# Revit family: Toilet-Waterworks-Alden
name_source: partatom
category: Plumbing Fixtures
revit_build: Autodesk Revit MEP 2014 (Build: 20140709_2115(x64)
units: mm (PartAtom-declared; Revit-internal decimal feet)

## types (24) — shared parameters
ADA Compliant = Yes
Assembly Code = D2010110
CW Connection = Yes
Certification IAPMO = Yes
Certification Watersense = Yes
Certification cUPC = Yes
Code Compliance = Complies with ASME 112.19.2-2008/CSA B45.1-08, WaterSense. Certified with IAPMO & cUPC
Cold Water Connector = Cold Water - Male Threading
Cold Water Diameter = 0' - 0 1/2"
Default Elevation = 0' - 0"
Depth = 2' - 5 1/4"
Flush Rate = 1.28 gpf
HW Connection = No
Height = 2' - 3 5/8"
Keynote = 22 40 00.E3
Length = 1' - 4 1/4"
Manufacturer = Waterworks
Model = ALWC01
Pressure = 45.00 psi
Product Documentation Link = http://assets.waterworks.com
Product Name = Alden One Piece High Efficiency Elongated Watercloset with Molded Wood Seat
Product Page URL = http://www.waterworks.com
Sanitary Connector = Waste Drain
Trapway Diameter = 0' - 2 1/8"
URL = http://www.waterworks.com
Vent Connection = Yes
Version = 2014 - v1.0a
Warranty = http://www.waterworks.com
Waste Connection = Yes
Waste Connection Diameter = 0' - 2 1/8"
Water Pressure = Max: 85psi / Min: 20psi / Recommended: 45psi
‌Installation Requirements or Notes = Waste Rough-In Depth: 1-2in from finished wall.  See Installation Guidelines

## per-type parameters (varying)
| type | Constraint | Description | Finish | Metal Finish | Model SKU |
| Bright White - Antique Brass  Lever | 1 | One Piece Elongated Watercloset in Bright White with Antique Brass Lever | Vitreous China - Waterworks - Bright White | Metal - Waterworks - Antique Brass | 14-08039-64466 |
| Bright White - Antique Copper  Lever | 2 | One Piece Elongated Watercloset in Bright White with Antique Copper Lever | Vitreous China - Waterworks - Bright White | Metal - Waterworks - Antique Copper | 14-01136-13871 |
| Bright White - Architectural Bronze  Lever | 3 | One Piece Elongated Watercloset in Bright White with Architectural Bronze Lever | Vitreous China - Waterworks - Bright White | Metal - Waterworks - Architectural Bronze | 14-38638-51317 |
| Bright White - Burnished Brass  Lever | 4 | One Piece Elongated Watercloset in Bright White with Burnished Brass Lever | Vitreous China - Waterworks - Bright White | Metal - Waterworks - Burnished Brass | 14-32651-23069 |
| Bright White - Burnished Nickel  Lever | 5 | One Piece Elongated Watercloset in Bright White with Burnished Nickel Lever | Vitreous China - Waterworks - Bright White | Metal - Waterworks - Burnished Nickel | 14-56783-33394 |
| Bright White - Carbon  Lever | 6 | One Piece Elongated Watercloset in Bright White with Carbon Lever | Vitreous China - Waterworks - Bright White | Metal - Waterworks - Carbon | 14-89032-34872 |
| Bright White - Chrome  Lever | 7 | One Piece Elongated Watercloset in Bright White with Chrome Lever | Vitreous China - Waterworks - Bright White | Metal - Waterworks - Chrome | 14-48096-60456 |
| Bright White - Gold  Lever | 8 | One Piece Elongated Watercloset in Bright White with Gold Lever | Vitreous China - Waterworks - Bright White | Metal - Waterworks - Gold | 14-45384-68425 |
| Bright White - Matte Gold  Lever | 9 | One Piece Elongated Watercloset in Bright White with Matte Gold Lever | Vitreous China - Waterworks - Bright White | Metal - Waterworks - Matte Gold | 14-83029-59346 |
| Bright White - Matte Nickel  Lever | 10 | One Piece Elongated Watercloset in Bright White with Matte Nickel Lever | Vitreous China - Waterworks - Bright White | Metal - Waterworks - Matte Nickel | 14-23729-66657 |
| Bright White - Nickel  Lever | 11 | One Piece Elongated Watercloset in Bright White with Nickel Lever | Vitreous China - Waterworks - Bright White | Metal - Waterworks - Nickel | 14-67965-18117 |
| Bright White - Pewter  Lever | 12 | One Piece Elongated Watercloset in Bright White with Pewter Lever | Vitreous China - Waterworks - Bright White | Metal - Waterworks - Pewter | 14-19227-72516 |
| Bright White - Shiny Copper  Lever | 13 | One Piece Elongated Watercloset in Bright White with Shiny Copper Lever | Vitreous China - Waterworks - Bright White | Metal - Waterworks - Shiny Copper | 14-49333-08937 |
| Bright White - Sovereign  Lever | 14 | One Piece Elongated Watercloset in Bright White with Sovereign Lever | Vitreous China - Waterworks - Bright White | Metal - Waterworks - Sovereign | 14-13856-87340 |
| Bright White - Unlacquered Brass  Lever | 15 | One Piece Elongated Watercloset in Bright White with Unlacquered Brass Lever | Vitreous China - Waterworks - Bright White | Metal - Waterworks - Unlacquered Brass | 14-20863-68530 |
| Bright White - Vintage Brass  Lever | 16 | One Piece Elongated Watercloset in Bright White with Vintage Brass Lever | Vitreous China - Waterworks - Bright White | Metal - Waterworks - Vintage Brass | 14-24975-15942 |
| Warm White - Antique Brass  Lever | 17 | One Piece Elongated Watercloset in Warm White with Antique Brass Lever | Vitreous China - Waterworks - Warm White | Metal - Waterworks - Antique Brass | 14-48433-00670 |
| Warm White - Antique Copper  Lever | 18 | One Piece Elongated Watercloset in Warm White with Antique Copper Lever | Vitreous China - Waterworks - Warm White | Metal - Waterworks - Antique Copper | 14-05963-72125 |
| Warm White - Architectural Bronze  Lever | 19 | One Piece Elongated Watercloset in Warm White with Architectural Bronze Lever | Vitreous China - Waterworks - Warm White | Metal - Waterworks - Architectural Bronze | 14-73966-92840 |
| Warm White - Chrome  Lever | 20 | One Piece Elongated Watercloset in Warm White with Chrome Lever | Vitreous China - Waterworks - Warm White | Metal - Waterworks - Chrome | 14-89498-03934 |
| Warm White - Matte Nickel  Lever | 21 | One Piece Elongated Watercloset in Warm White with Matte Nickel Lever | Vitreous China - Waterworks - Warm White | Metal - Waterworks - Matte Nickel | 14-15269-71210 |
| Warm White - Nickel  Lever | 22 | One Piece Elongated Watercloset in Warm White with Nickel Lever | Vitreous China - Waterworks - Warm White | Metal - Waterworks - Nickel | 14-09129-39575 |
| Warm White - Sovereign  Lever | 23 | One Piece Elongated Watercloset in Warm White with Sovereign Lever | Vitreous China - Waterworks - Warm White | Metal - Waterworks - Sovereign | 14-17423-91521 |
| Warm White - Unlacquered Brass  Lever | 24 | One Piece Elongated Watercloset in Warm White with Unlacquered Brass Lever | Vitreous China - Waterworks - Warm White | Metal - Waterworks - Unlacquered Brass | 14-61670-68410 |

## geometry (parser evidence)
native form markers: Sweep x1
no freeform markers — native parametric forms only
